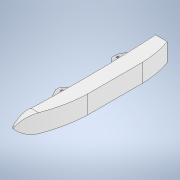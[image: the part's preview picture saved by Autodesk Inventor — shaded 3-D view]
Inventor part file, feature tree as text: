
AUTODESK INVENTOR PART (.ipt)
format: ipt  version: 2020 (Build 240168000, 168)  size: 535,040 bytes
history: native  units: mm
features: sketch x9, extrude x8, fillet x4, chamfer x2, hole x1, shell x1
ambient origin geometry x8: Origin, YZ Plane, XZ Plane, XY Plane, X Axis, Y Axis, Z Axis, Center Point
bodies: Volumenkörper1 (feature_tree)
feature tree (25):
  extrude  "Extrusion1"  Depth=386.0mm
  extrude  "Extrusion2"  Depth=310.0mm TaperAngle=0.0deg
  extrude  "Extrusion4"  Depth=71.0mm
  extrude  "Extrusion7"  Depth=970.0mm
  extrude  "Extrusion8"  Depth=40.0mm
  extrude  "Extrusion9"  Depth=310.0mm TaperAngle=0.0deg
  chamfer  "Fase1"  Distance=52.0mm
  chamfer  "Fase2"  Distance=52.0mm
  extrude  "Extrusion11"  Depth=15.0mm
  extrude  "Extrusion10"  Depth=15.0mm
  fillet  "Rundung3"  Radius=15.0mm
  hole  "Bohrung1"  [1 undecoded]
  fillet  "Rundung4"  Radius=15.0mm
  fillet  "Rundung5"  Radius=317.5mm
  fillet  "Rundung6"  Radius=188.2mm
  shell  "Wandung2"  Thickness=79.4mm
  sketch  "Skizze1"  dims[d0=2439.0mm d1=386.0mm]
  sketch  "Skizze2"  dims[d2=2439.0mm d3=310.0mm d4=0.0mm]
  sketch  "Skizze4"  dims[d5=871.0mm d7=71.0mm]
  sketch  "Skizze9"  dims[d8=40.0mm d9=970.0mm]
  sketch  "Skizze10"  dims[d10=51.0mm d11=40.0mm]
  sketch  "Skizze11"  dims[d12=310.0mm d13=0.0mm d21=310.0mm d22=0.0mm]
  sketch  "Skizze12"  dims[d31=298.0mm]
  sketch  "Skizze17"  dims[d32=307.0mm]
  sketch  "Skizze20"  dims[d33=43.5mm d34=52.0mm d35=0.0mm d36=52.0mm d37=0.0mm d38=326.0mm d39=101.786531mm d40=15.0mm d41=15.0mm d42=15.0mm d43=317.5mm d44=188.2mm d45=79.4mm d46=91.2mm d47=675.4mm d49=113.2mm d50=88.2mm d51=166.1mm d52=310.0mm d53=0.0mm d54=15.0mm d55=1132.66mm d56=310.0mm d57=0.0mm d58=319.363mm d59=103.0mm d60=22.5deg d61=319.363mm d62=103.0mm d63=22.5deg d66=390.0mm d67=390.0mm d68=310.0mm d69=0.0mm d70=30.0mm d72=5.0mm d77=50.0mm d78=50.0mm d79=100.0mm d80=5.0mm d81=6.0mm d82=4.0mm d83=2.0mm d84=90.0deg d85=100.0mm d86=20.594885mm d87=15.0mm d88=15.0mm d89=15.0mm]
note: 1 required parameter value undecoded (feature->parameter linkage not recoverable at this tier; creation-order binding heuristic only, values carry confidence <= 0.55)
